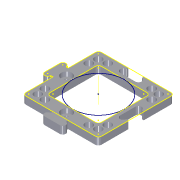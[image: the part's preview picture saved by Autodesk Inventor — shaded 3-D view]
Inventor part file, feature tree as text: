
AUTODESK INVENTOR PART (.ipt)
format: ipt  version: 2022 (Build 260153000, 153)  size: 419,328 bytes
history: native  units: mm
features: sketch x6, projected_geometry x5, extrude x4, mirror x2, pattern_circular x2, other x1, hole x1
ambient origin geometry x8: Origin, YZ Plane, XZ Plane, XY Plane, X Axis, Y Axis, Z Axis, Center Point
bodies: Volumenkörper1 (feature_tree)
feature tree (21):
  extrude  "Extrusion1"  TaperAngle=0.0deg  [1 undecoded]
  mirror  "Mirror6"
  mirror  "Mirror7"
  extrude  "Extrusion13"  TaperAngle=0.0deg  [1 undecoded]
  sketch  "Sketch27"  dims[d9=0.0mm d13=0.0mm]
  extrude  "Extrusion14"  TaperAngle=0.0deg  [1 undecoded]
  other  "Work Axis4"
  pattern_circular  "Circular Pattern6"  [2 undecoded]
  hole  "Hole7"  [1 undecoded]
  extrude  "Extrusion15"  TaperAngle=0.0deg  [1 undecoded]
  pattern_circular  "Circular Pattern7"  [2 undecoded]
  sketch  "Skizze1"  dims[d5=0.0mm d6=0.0mm]
  sketch  "Sketch26"  dims[d7=0.0mm d8=0.0mm]
  projected_geometry  "Projected Loop21"
  projected_geometry  "Projected Loop22"
  sketch  "Sketch28"  dims[d14=0.0mm]
  projected_geometry  "Projected Loop23"
  sketch  "Sketch29"  dims[d20=0.0mm]
  projected_geometry  "Projected Loop24"
  sketch  "Sketch30"  dims[d21=0.0mm d22=0.0mm d23=0.0mm d24=0.0mm d25=3.0mm d26=0.0mm d27=0.0mm d28=0.0mm d29=0.0mm d30=0.0mm d31=0.0mm d32=0.0mm d33=0.0mm d34=0.0mm d46=0.0mm d47=0.0mm d48=0.0mm d49=-10.0mm d50=0.0mm d51=0.0mm d52=0.0mm d53=0.0mm d54=0.0mm d55=0.0mm d56=0.0mm d57=0.0mm d58=0.0mm d59=0.0mm d77=2.65mm d82=2.65mm d222=0.5mm d236=5.3mm d278=25.0mm d279=25.0mm d2=8.0mm d281=8.0mm d282=2.0mm d283=4.9mm d284=20.0mm d4=20.0mm d286=5.0mm d290=20.8mm d292=2.0mm d293=5.5mm d294=14.0mm d295=18.0mm d296=10.0mm d297=1.5mm d298=10.0mm d299=0.0mm d300=2.0mm d301=0.5mm d302=10.0mm d303=0.0mm d308=20.0mm d309=90.0deg d313=6.3mm d314=6.3mm d319=7.78mm d320=4.0mm d322=4.0mm d323=3.2mm d324=6.0mm d325=7.0mm d326=3.0mm d327=90.0deg d328=8.0mm d329=20.594885mm d330=0.0mm d331=0.0mm d332=0.0mm d334=14.0mm d336=10.0mm d337=1.5mm d338=2.0mm d339=0.5mm d340=0.075mm d341=0.075mm d342=0.075mm d343=0.075mm d344=10.0mm d345=0.0mm d346=0.075mm d347=0.0mm d348=20.0mm d349=90.0deg d354=0.075mm d355=3.5mm d356=10.15mm]
  projected_geometry  "Projected Loop25"
note: 9 required parameter values undecoded (feature->parameter linkage not recoverable at this tier; creation-order binding heuristic only, values carry confidence <= 0.55)
